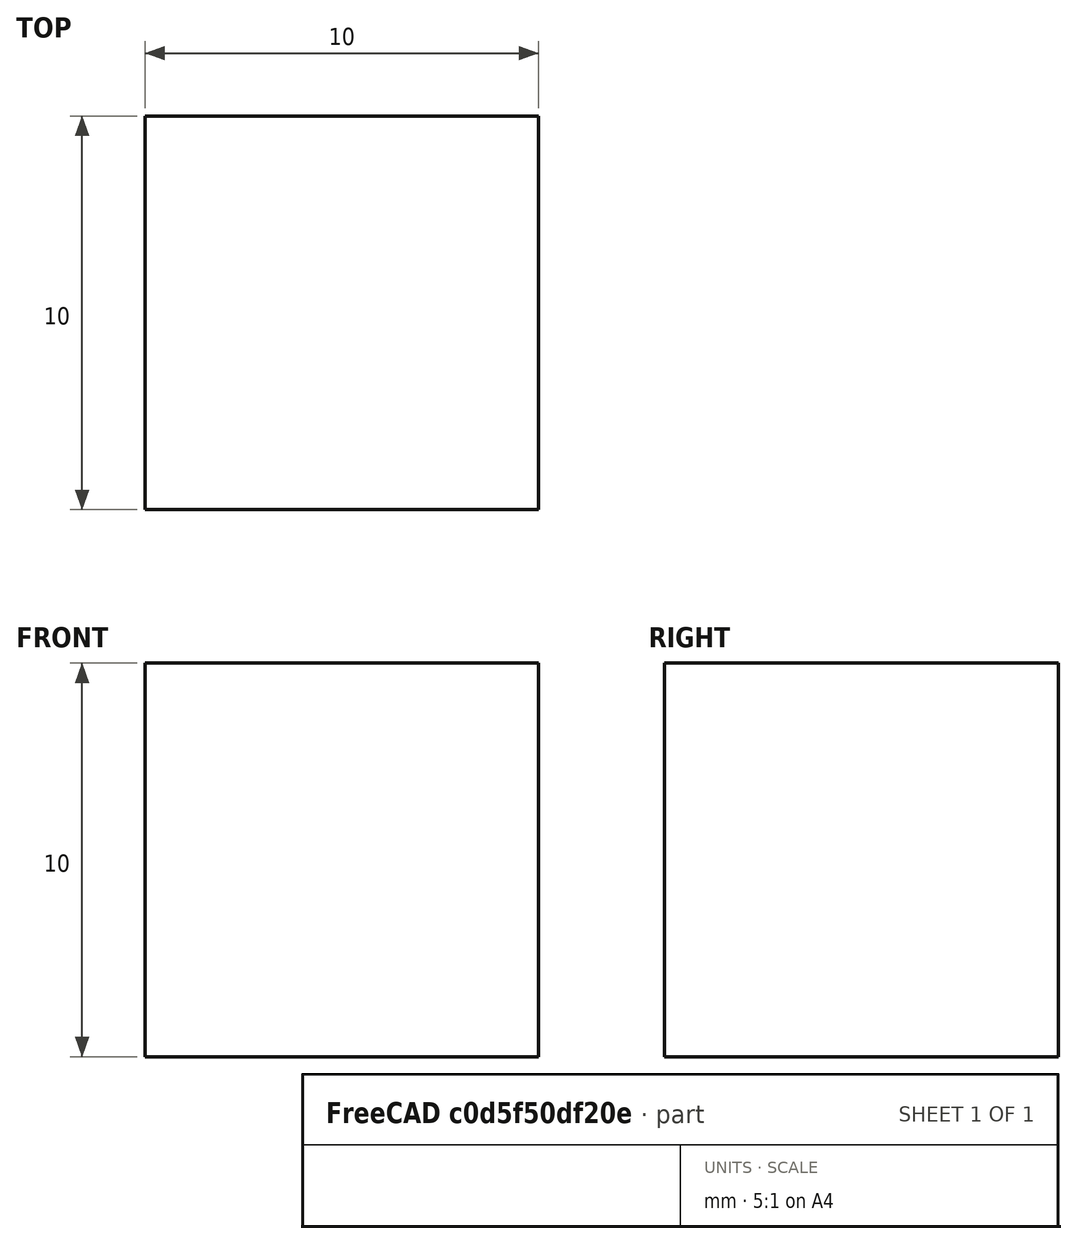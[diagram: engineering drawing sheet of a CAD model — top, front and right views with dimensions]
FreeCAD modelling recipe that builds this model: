
FCSTD DOCUMENT  (FreeCAD 1.0R39109 (Git))
Label: LED Board
License: All rights reserved
LicenseURL: http://en.wikipedia.org/wiki/All_rights_reserved
objects: App::VRMLObject×1, Part::Part2DObjectPython×1, Part::Box×1
note: 2 computed .brp shape members not serialized (recipe doc carries the construction recipe); baked Part::Feature solids carry a one-line shape summary decoded from their .brp

FEATURE [App::VRMLObject] LED_Board  label="LED Board"
  Resources = LED_Board/shapes3D/R_0603_1608Metric.wrl | LED_Board/shapes3D/PinSocket_1x03_P2.54mm_Horizontal.wrl | LED_Board/shapes3D/PinSocket_1x03_P2.54mm_Vertical.wrl | LED_Board/shapes3D/SOT-23-3P_L2.9-W1.3-H1.0-LS2.4-P0.95.wrl | LED_Board/shapes3D/C_0805_2012Metric.wrl | LED_Board/shapes3D/D_SMA.wrl | LED_Board/shapes3D/CP_Elec_8x10.wrl | LED_Board/shapes3D/IDC-Header_2x05_P2.54mm_Vertical.wrl | LED_Board/shapes3D/TO-263-3_L10.2-W9.2-P5.08-LS15.4-BR.wrl | LED_Board/shapes3D/TSSOP-20_4.4x6.5mm_P0.65mm.wrl | LED_Board/shapes3D/CONN-TH_XT60PW-M.wrl
FEATURE [Part::Part2DObjectPython] Rectangle  # Draft 2D object (typed FeaturePython)
  Area = 6538.64
  ChamferSize = 0
  Columns = 1
  FilletRadius = 0
  Height = 59.8377
  Length = 109.273
  MakeFace = true
  Placement = pos=(63.6849,-91.0032,0) rot=(0,0,1;0rad)
  Rows = 1
FEATURE [Part::Box] Box  label="Cube"
  AttacherType = Attacher::AttachEngine3D
  Height = 10
  Length = 10
  Placement = pos=(63.36,-90.76,0) rot=(0,0,1;0rad)
  Width = 10
